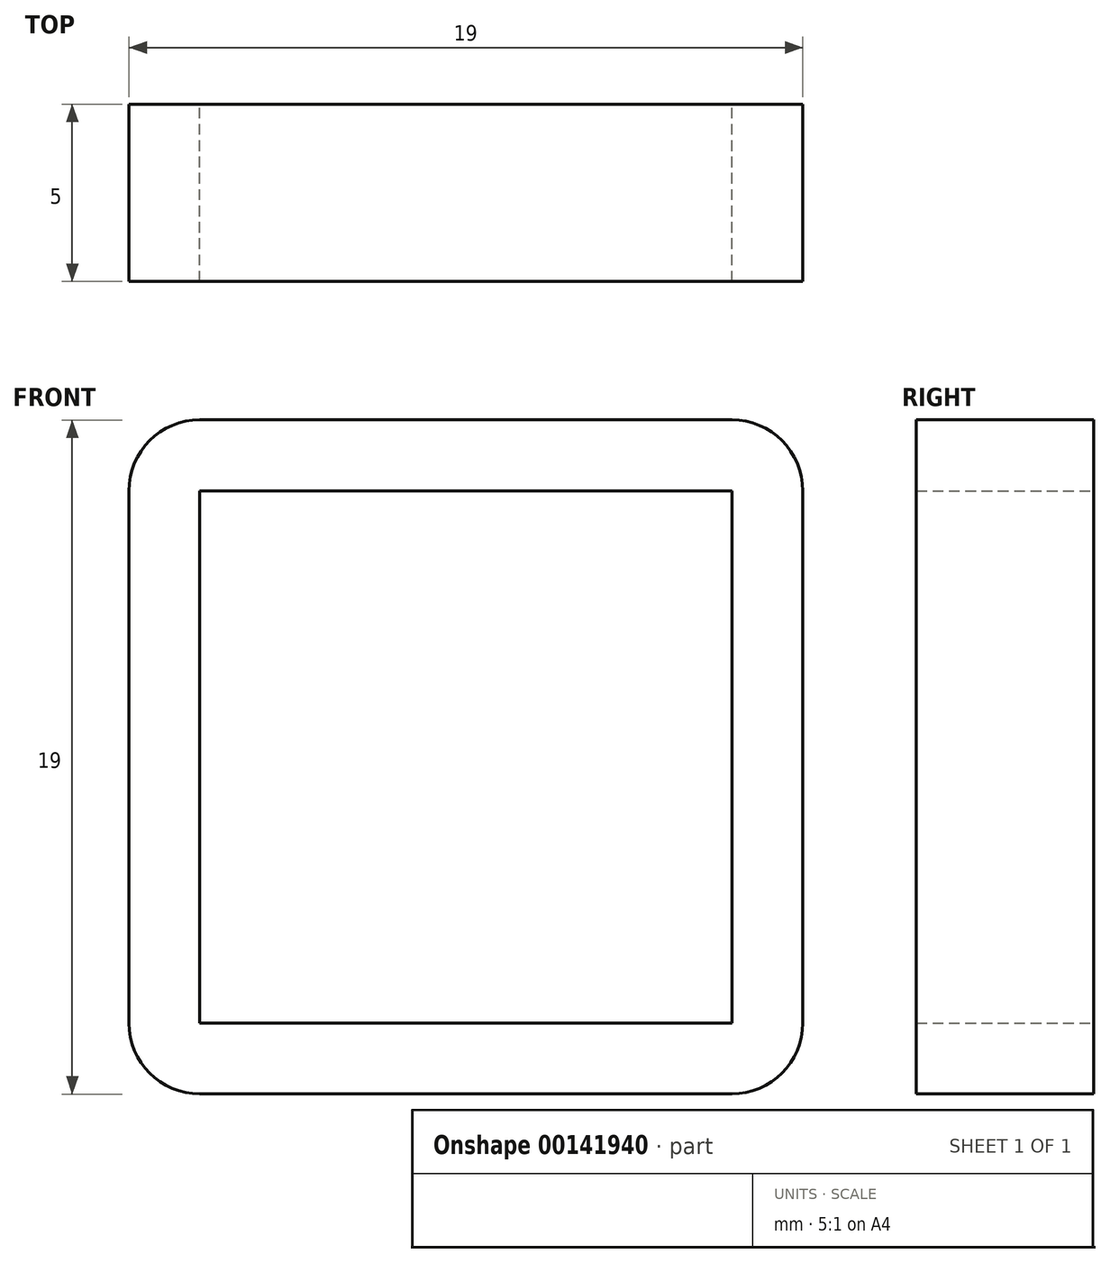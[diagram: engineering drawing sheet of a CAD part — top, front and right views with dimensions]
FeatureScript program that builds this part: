
annotation { "Feature Type Name" : "Feature", "Feature Type Description" : "" }
export const myFeature = defineFeature(function(context is Context, id is Id, definition is map)
    precondition{}
    {
        {
            var Q0;
            Q0=qCreatedBy(makeId("Front.planeOp"),FACE);
            var sketch = newSketch(context, id + "F0", { "sketchPlane" : qUnion([Q0])});
            skLineSegment(sketch, "E0.bottom", {"start": v(-3.1, 2.31) * mm, "end": v(11.9, 2.31) * mm});
            skLineSegment(sketch, "E0.top", {"start": v(-3.1, -12.69) * mm, "end": v(11.9, -12.69) * mm});
            skLineSegment(sketch, "E0.left", {"start": v(-3.1, 2.31) * mm, "end": v(-3.1, -12.69) * mm});
            skLineSegment(sketch, "E0.right", {"start": v(11.9, 2.31) * mm, "end": v(11.9, -12.69) * mm});
            skLineSegment(sketch, "E1.bottom", {"start": v(-5.1, 4.31) * mm, "end": v(13.9, 4.31) * mm});
            skLineSegment(sketch, "E1.top", {"start": v(-5.1, -14.69) * mm, "end": v(13.9, -14.69) * mm});
            skLineSegment(sketch, "E1.left", {"start": v(-5.1, 4.31) * mm, "end": v(-5.1, -14.69) * mm});
            skLineSegment(sketch, "E1.right", {"start": v(13.9, 4.31) * mm, "end": v(13.9, -14.69) * mm});
            skSolve(sketch);
        }
        {
            var Q0;
            Q0=makeQuery(id+"F0.imprint","IMPRINT",FACE,{"disambiguationData":[TD([[makeQuery(id+"F0.imprint","IMPRINT",EDGE,{"derivedFrom":sQuery(id+"F0.wireOp",EDGE,"E0.bottom")}),1.0]])]});
            extrude(context, id + "F1", {"entities" : qUnion([Q0]), "depth" : 5 * mm, "offsetDistance" : 25 * mm});
        }
        {
            var Q0;
            Q0=makeQuery(id+"F1.opExtrude","SWEPT_EDGE",EDGE,{"disambiguationData":[OSD([sQuery(id+"F0.wireOp",EDGE,"E1.bottom"),sQuery(id+"F0.wireOp",EDGE,"E1.right")])]});
            var Q1;
            Q1=makeQuery(id+"F1.opExtrude","SWEPT_EDGE",EDGE,{"disambiguationData":[OSD([sQuery(id+"F0.wireOp",EDGE,"E1.top"),sQuery(id+"F0.wireOp",EDGE,"E1.right")])]});
            var Q2;
            Q2=makeQuery(id+"F1.opExtrude","SWEPT_EDGE",EDGE,{"disambiguationData":[OSD([sQuery(id+"F0.wireOp",EDGE,"E1.top"),sQuery(id+"F0.wireOp",EDGE,"E1.left")])]});
            var Q3;
            Q3=makeQuery(id+"F1.opExtrude","SWEPT_EDGE",EDGE,{"disambiguationData":[OSD([sQuery(id+"F0.wireOp",EDGE,"E1.bottom"),sQuery(id+"F0.wireOp",EDGE,"E1.left")])]});
            fillet(context, id + "F2", {"entities" : qUnion([Q0, Q1, Q2, Q3]), "radius" : 2 * mm, "tangentPropagation" : true, "allowEdgeOverflow" : false});
        }
    });
